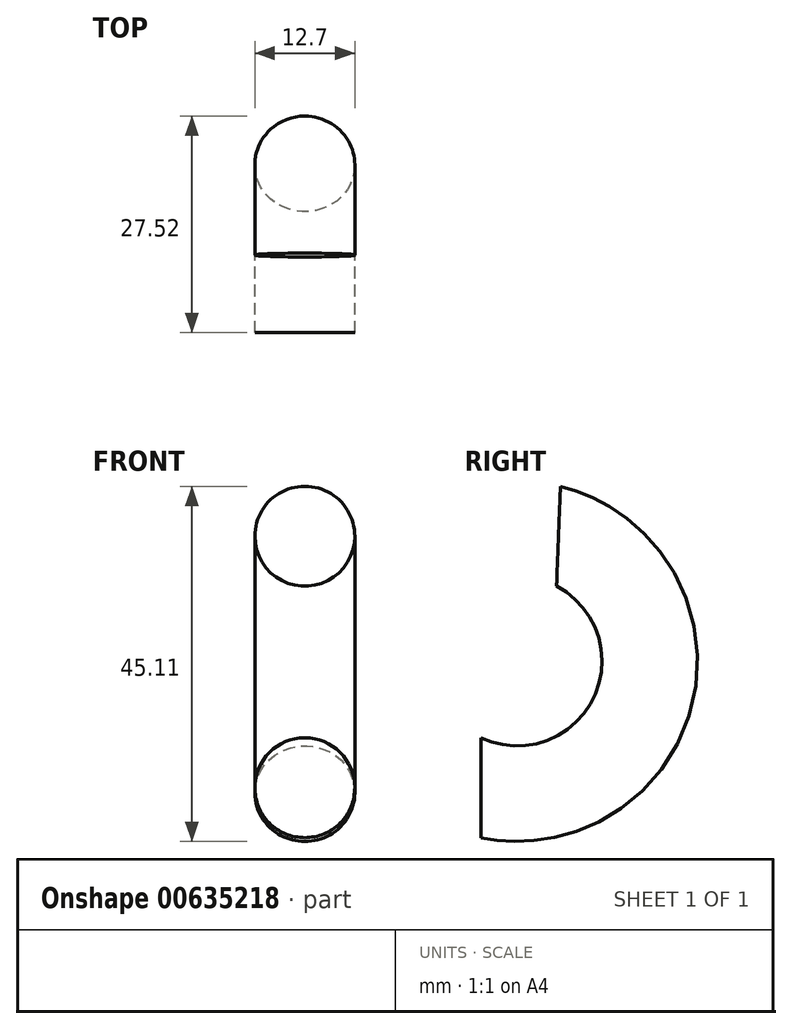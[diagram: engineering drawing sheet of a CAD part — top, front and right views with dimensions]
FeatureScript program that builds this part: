
annotation { "Feature Type Name" : "Feature", "Feature Type Description" : "" }
export const myFeature = defineFeature(function(context is Context, id is Id, definition is map)
    precondition{}
    {
        {
            var Q0;
            Q0=qCreatedBy(makeId("Right.planeOp"),FACE);
            var sketch = newSketch(context, id + "F0", { "sketchPlane" : qUnion([Q0])});
            skLineSegment(sketch, "E0", {"start": v(0, 0) * mm, "end": v(4.63, 0) * mm});
            skArc(sketch, "E1", {"start": v(4.63, 0) * mm, "mid": v(20.7, 15.76) * mm, "end": v(5.24, 32.12) * mm});
            skSolve(sketch);
        }
        {
            var Q0;
            Q0=qCreatedBy(makeId("Front.planeOp"),FACE);
            var sketch = newSketch(context, id + "F1", { "sketchPlane" : qUnion([Q0])});
            skCircle(sketch, "E2", {"center": v(0, 0) * mm, "radius": 6.35 * mm});
            skSolve(sketch);
        }
        {
            var Q0;
            Q0=makeQuery(id+"F1.imprint","IMPRINT",FACE,{"disambiguationData":[TD([[makeQuery(id+"F1.imprint","IMPRINT",EDGE,{"derivedFrom":sQuery(id+"F1.wireOp",EDGE,"E2")}),1.0]])]});
            var Q1;
            Q1=sQuery(id+"F0.wireOp",EDGE,"E1");
            sweep(context, id + "F2", {"profiles" : qUnion([Q0]), "path" : qUnion([Q1])});
        }
    });
